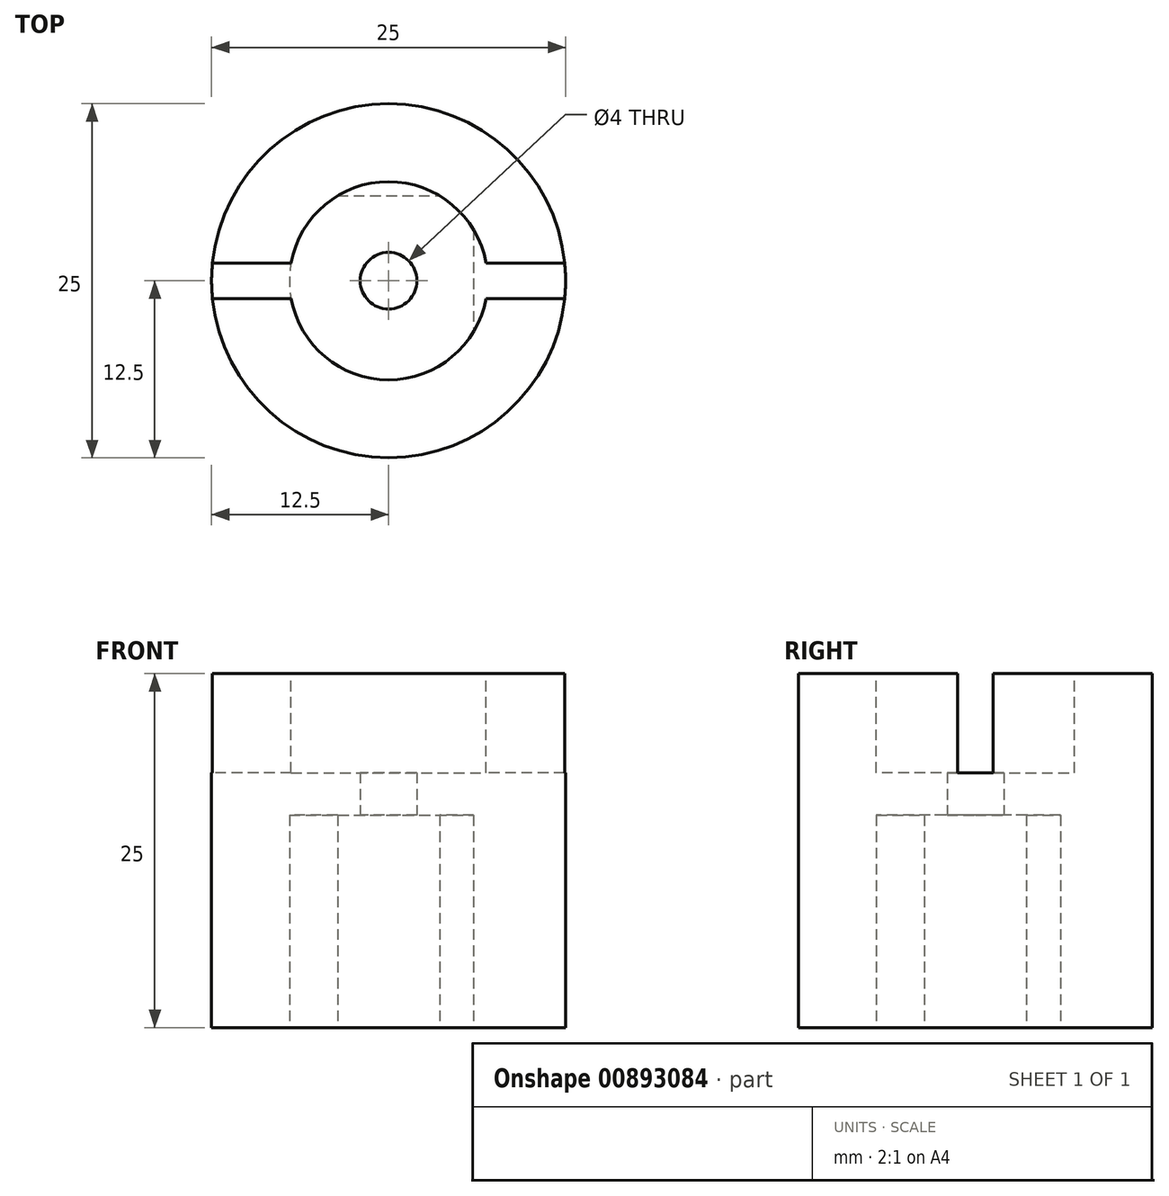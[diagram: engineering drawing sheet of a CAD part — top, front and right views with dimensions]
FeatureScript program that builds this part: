
annotation { "Feature Type Name" : "Feature", "Feature Type Description" : "" }
export const myFeature = defineFeature(function(context is Context, id is Id, definition is map)
    precondition{}
    {
        {
            var Q0;
            Q0=qCreatedBy(makeId("Top.planeOp"),FACE);
            var sketch = newSketch(context, id + "F0", { "sketchPlane" : qUnion([Q0])});
            skPoint(sketch, "E0.middle", {"position": v(0, 0) * mm});
            skArc(sketch, "E1", {"start": v(-3.6, 6) * mm, "mid": v(-4.95, -4.95) * mm, "end": v(6, -3.6) * mm});
            skLineSegment(sketch, "E2.bottom", {"start": v(-3.6, 6) * mm, "end": v(3.6, 6) * mm});
            skLineSegment(sketch, "E2.right", {"start": v(6, 3.6) * mm, "end": v(6, -3.6) * mm});
            skPoint(sketch, "E3.orphan", {"position": v(-6, 6) * mm});
            skPoint(sketch, "E2.left.end.orphan", {"position": v(-6, -6) * mm});
            skPoint(sketch, "E4.orphan", {"position": v(6, -6) * mm});
            skArc(sketch, "E5.trimOffspring", {"start": v(6, 3.6) * mm, "mid": v(4.95, 4.95) * mm, "end": v(3.6, 6) * mm});
            skPoint(sketch, "E6.orphan", {"position": v(6, 6) * mm});
            skCircle(sketch, "E7", {"center": v(0, 0) * mm, "radius": 2 * mm});
            skSolve(sketch);
        }
        {
            var Q0;
            Q0=qCreatedBy(makeId("Top.planeOp"),FACE);
            var sketch = newSketch(context, id + "F1", { "sketchPlane" : qUnion([Q0])});
            skCircle(sketch, "E8", {"center": v(0, 0) * mm, "radius": 12.5 * mm});
            skCircle(sketch, "E9", {"center": v(0, 0) * mm, "radius": 2 * mm});
            skSolve(sketch);
        }
        {
            var Q0;
            Q0 = qSketchRegion(id + "F1", true);
            extrude(context, id + "F2", {"entities" : qUnion([Q0]), "depth" : 25 * mm, "offsetDistance" : 25 * mm});
        }
        {
            var Q0;
            Q0=makeQuery(id+"F0.imprint","IMPRINT",FACE,{"disambiguationData":[TD([[makeQuery(id+"F0.imprint","IMPRINT",EDGE,{"derivedFrom":sQuery(id+"F0.wireOp",EDGE,"E1")}),1.0]])]});
            extrude(context, id + "F3", {"entities" : qUnion([Q0]), "operationType" : NewBodyOperationType.REMOVE, "depth" : 15 * mm, "offsetDistance" : 25 * mm});
        }
        {
            var Q0;
            Q0=makeQuery(id+"F2.opExtrude","CAP_FACE",FACE,{"disambiguationData":[OSD([sQuery(id+"F1.wireOp",EDGE,"E8"),sQuery(id+"F1.wireOp",EDGE,"E9")])],"isStart":false});
            var sketch = newSketch(context, id + "F4", { "sketchPlane" : qUnion([Q0])});
            skArc(sketch, "E10", {"start": v(-12.44, 1.25) * mm, "mid": v(-12.5, 0) * mm, "end": v(-12.44, -1.25) * mm});
            skArc(sketch, "E11", {"start": v(-6.89, -1.25) * mm, "mid": v(0, -7) * mm, "end": v(6.89, -1.25) * mm});
            skLineSegment(sketch, "E12.bottom", {"start": v(12.44, -1.25) * mm, "end": v(6.89, -1.25) * mm});
            skLineSegment(sketch, "E12.top", {"start": v(12.44, 1.25) * mm, "end": v(6.89, 1.25) * mm});
            skLineSegment(sketch, "E12.left", {"start": v(12.44, -1.25) * mm, "end": v(12.44, 1.25) * mm});
            skLineSegment(sketch, "E12.right", {"start": v(-12.44, -1.25) * mm, "end": v(-12.44, 1.25) * mm});
            skLineSegment(sketch, "E13.trimOffspring", {"start": v(-6.89, 1.25) * mm, "end": v(-12.44, 1.25) * mm});
            skLineSegment(sketch, "E14.trimOffspring", {"start": v(-6.89, -1.25) * mm, "end": v(-12.44, -1.25) * mm});
            skArc(sketch, "E15.trimOffspring", {"start": v(6.89, 1.25) * mm, "mid": v(0, 7) * mm, "end": v(-6.89, 1.25) * mm});
            skArc(sketch, "E16.trimOffspring", {"start": v(12.44, -1.25) * mm, "mid": v(12.5, 0) * mm, "end": v(12.44, 1.25) * mm});
            skSolve(sketch);
        }
        {
            var Q0;
            Q0 = qSketchRegion(id + "F4", true);
            extrude(context, id + "F5", {"entities" : qUnion([Q0]), "operationType" : NewBodyOperationType.REMOVE, "oppositeDirection" : true, "depth" : 7 * mm, "offsetDistance" : 25 * mm});
        }
    });
